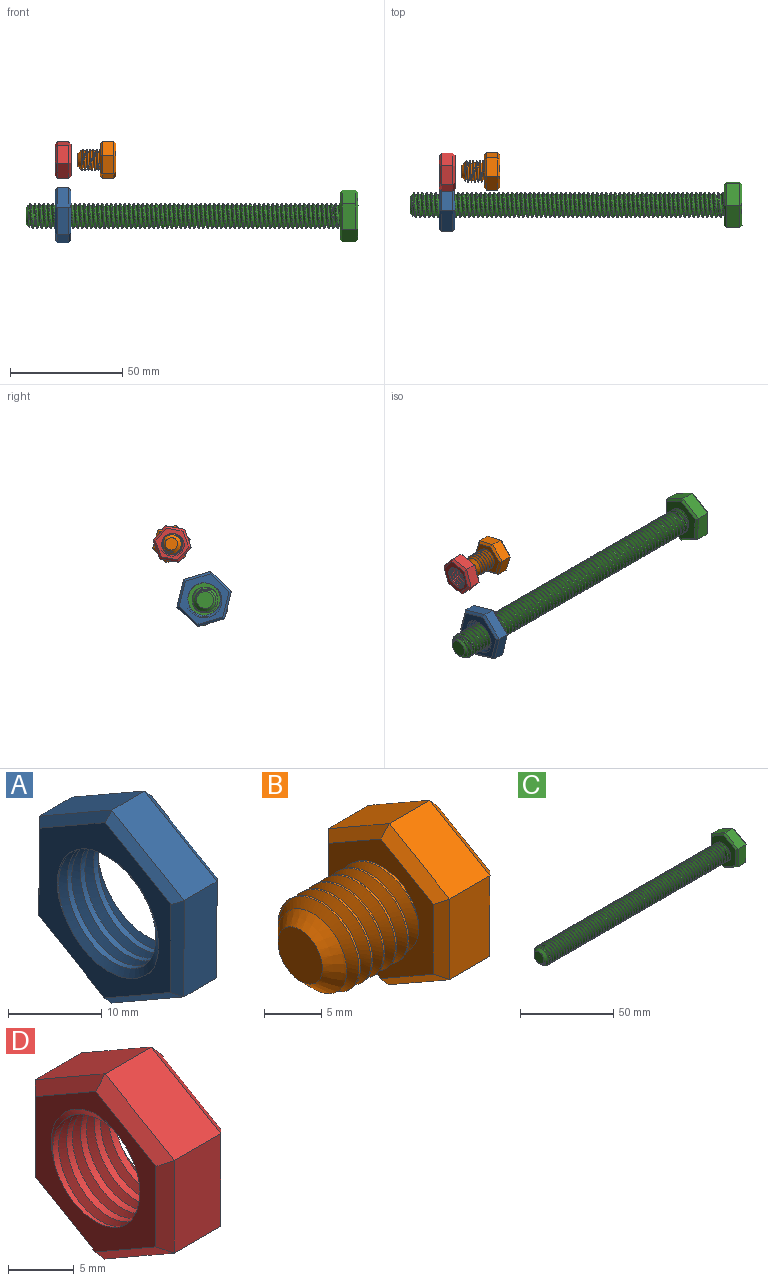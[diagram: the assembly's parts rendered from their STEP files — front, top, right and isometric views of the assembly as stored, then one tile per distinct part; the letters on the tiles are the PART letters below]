
ASSEMBLY  parts=4 mates=2
PART A: 23 faces, bbox 9.3x22.7x26 mm
  f0: cylinder r=7.24mm len=14.48mm, axis (1,0,0), area 111.6mm2, adj f7,f8,f21,f22
  f1: plane 10.98x6.38mm, normal (0,-0.5,0.86), area 63.5mm2, adj f2,f6,f14,f18
  f2: plane 12.7x5mm, normal (0,-1,0), area 63.5mm2, adj f1,f3,f12,f16
  f3: plane 11.02x6.32mm, normal (0,-0.5,-0.87), area 63.5mm2, adj f2,f4,f10,f15
  f4: plane 10.98x6.38mm, normal (0,0.5,-0.86), area 63.5mm2, adj f3,f5,f9,f17
  f5: plane 12.7x5mm, normal (0,1,0), area 63.5mm2, adj f4,f6,f11,f19
  f6: plane 11.02x6.32mm, normal (0,0.5,0.87), area 63.5mm2, adj f1,f5,f13,f20
  f7: plane 23.73x20.67mm, normal (-1,0,0), area 164.4mm2, adj f0,f9,f10,f11,f12,f13,f14,f21
  f8: plane 23.73x20.67mm, normal (1,0,0), area 164.4mm2, adj f0,f15,f16,f17,f18,f19,f20,f21
  f9: plane 10.99x6.96mm, normal (-0.71,0.36,-0.61), area 17.1mm2, adj f4,f7,f10,f11
  f10: plane 11.02x6.9mm, normal (-0.71,-0.35,-0.61), area 17.1mm2, adj f3,f7,f9,f12
  f11: plane 12.7x1.03mm, normal (-0.71,0.71,0), area 17.1mm2, adj f5,f7,f9,f13
  f12: plane 12.7x1.03mm, normal (-0.71,-0.71,0), area 17.1mm2, adj f2,f7,f10,f14
  f13: plane 11.02x6.9mm, normal (-0.71,0.35,0.61), area 17.1mm2, adj f6,f7,f11,f14
  f14: plane 10.99x6.96mm, normal (-0.71,-0.36,0.61), area 17.1mm2, adj f1,f7,f12,f13
  f15: plane 11.02x6.9mm, normal (0.71,-0.35,-0.61), area 17.1mm2, adj f3,f8,f16,f17
  f16: plane 12.7x1.03mm, normal (0.71,-0.71,0), area 17.1mm2, adj f2,f8,f15,f18
  f17: plane 10.99x6.96mm, normal (0.71,0.36,-0.61), area 17.1mm2, adj f4,f8,f15,f19
  f18: plane 10.99x6.96mm, normal (0.71,-0.36,0.61), area 17.1mm2, adj f1,f8,f16,f20
  f19: plane 12.7x1.03mm, normal (0.71,0.71,0), area 17.1mm2, adj f5,f8,f17,f20
  f20: plane 11.02x6.9mm, normal (0.71,0.35,0.61), area 17.1mm2, adj f6,f8,f18,f19
  f21: bspline ~19.31x16.73mm, area 223mm2, adj f0,f7,f8,f22
  f22: bspline ~19.31x16.73mm, area 223mm2, adj f0,f7,f8,f21
PART B: 25 faces, bbox 17.8x15.9x18.1 mm
  f0: cylinder r=4.75mm len=9.5mm, axis (1,0,0), area 28.1mm2, adj f1,f2,f4,f12
  f1: bspline ~10.97x9.91mm, area 196.7mm2, adj f0,f2,f4,f12
  f2: bspline ~10.97x10.66mm, area 196.6mm2, adj f0,f1,f4,f12
  f3: plane 5.5x5.5mm, normal (-1,0,0), area 23.8mm2, adj f4
  f4: cone r=4.75mm half-angle=45deg, axis (1,0,0), area 47.4mm2, adj f0,f1,f2,f3
  f5: plane 7.48x5mm, normal (0,-0.5,0.86), area 43.3mm2, adj f6,f10,f18,f22
  f6: plane 8.66x5mm, normal (0,-1,0), area 43.3mm2, adj f5,f7,f16,f20
  f7: plane 7.52x5mm, normal (0,-0.5,-0.87), area 43.3mm2, adj f6,f8,f14,f19
  f8: plane 7.48x5mm, normal (0,0.5,-0.86), area 43.3mm2, adj f7,f9,f13,f21
  f9: plane 8.66x5mm, normal (0,1,0), area 43.3mm2, adj f8,f10,f15,f23
  f10: plane 7.52x5mm, normal (0,0.5,0.87), area 43.3mm2, adj f5,f9,f17,f24
  f11: plane 15.01x13.03mm, normal (1,0,0), area 146.4mm2, adj f13,f14,f15,f16,f17,f18
  f12: plane 15.83x13.85mm, normal (-1,0,0), area 89.2mm2, adj f0,f1,f2,f19,f20,f21,f22,f23
  f13: plane 7.49x4.93mm, normal (0.71,0.36,-0.61), area 11.4mm2, adj f8,f11,f14,f15
  f14: plane 7.52x4.88mm, normal (0.71,-0.35,-0.61), area 11.4mm2, adj f7,f11,f13,f16
  f15: plane 8.66x1.03mm, normal (0.71,0.71,0), area 11.4mm2, adj f9,f11,f13,f17
  f16: plane 8.66x1.03mm, normal (0.71,-0.71,0), area 11.4mm2, adj f6,f11,f14,f18
  f17: plane 7.52x4.88mm, normal (0.71,0.35,0.61), area 11.4mm2, adj f10,f11,f15,f18
  f18: plane 7.49x4.93mm, normal (0.71,-0.36,0.61), area 11.4mm2, adj f5,f11,f16,f17
  f19: plane 7.52x4.88mm, normal (-0.71,-0.35,-0.61), area 11.4mm2, adj f7,f12,f20,f21
  f20: plane 8.66x1.03mm, normal (-0.71,-0.71,0), area 11.4mm2, adj f6,f12,f19,f22
  f21: plane 7.49x4.93mm, normal (-0.71,0.36,-0.61), area 11.4mm2, adj f8,f12,f19,f23
  f22: plane 7.49x4.93mm, normal (-0.71,-0.36,0.61), area 11.4mm2, adj f5,f12,f20,f24
  f23: plane 8.66x1.03mm, normal (-0.71,0.71,0), area 11.4mm2, adj f9,f12,f21,f24
  f24: plane 7.52x4.88mm, normal (-0.71,0.35,0.61), area 11.4mm2, adj f10,f12,f22,f23
PART C: 26 faces, bbox 149.6x21.1x24.2 mm
  f0: cylinder r=5.76mm len=138mm, axis (1,0,0), area -230.5mm2, adj f1,f2,f4,f5,f13
  f1: bspline ~140.88x13.3mm, area 3820.7mm2, adj f0,f2,f4,f5,f13
  f2: bspline ~141.54x13.3mm, area 3821.3mm2, adj f0,f1,f4,f13
  f3: plane 7.52x7.52mm, normal (-1,0,0), area 44.4mm2, adj f4
  f4: cone r=5.76mm half-angle=45deg, axis (1,0,0), area 53.1mm2, adj f0,f1,f2,f3,f5
  f5: cone r=5.76mm half-angle=45deg, axis (1,0,0), area 0.5mm2, adj f0,f1,f4
  f6: plane 9.98x6mm, normal (0,-0.5,0.86), area 69.3mm2, adj f7,f11,f19,f23
  f7: plane 11.55x6mm, normal (0,-1,0), area 69.3mm2, adj f6,f8,f17,f21
  f8: plane 10.02x6mm, normal (0,-0.5,-0.87), area 69.3mm2, adj f7,f9,f15,f20
  f9: plane 9.98x6mm, normal (0,0.5,-0.86), area 69.3mm2, adj f8,f10,f14,f22
  f10: plane 11.55x6mm, normal (0,1,0), area 69.3mm2, adj f9,f11,f16,f24
  f11: plane 10.02x6mm, normal (0,0.5,0.87), area 69.3mm2, adj f6,f10,f18,f25
  f12: plane 20.78x18.04mm, normal (1,0,0), area 280.6mm2, adj f14,f15,f16,f17,f18,f19
  f13: plane 21.88x19.13mm, normal (-1,0,0), area 198.3mm2, adj f0,f1,f2,f20,f21,f22,f23,f24
  f14: plane 9.98x6.38mm, normal (0.71,0.36,-0.61), area 15.5mm2, adj f9,f12,f15,f16
  f15: plane 10.02x6.32mm, normal (0.71,-0.35,-0.61), area 15.5mm2, adj f8,f12,f14,f17
  f16: plane 11.55x1.04mm, normal (0.71,0.71,0), area 15.5mm2, adj f10,f12,f14,f18
  f17: plane 11.55x1.04mm, normal (0.71,-0.71,0), area 15.5mm2, adj f7,f12,f15,f19
  f18: plane 10.02x6.32mm, normal (0.71,0.35,0.61), area 15.5mm2, adj f11,f12,f16,f19
  f19: plane 9.98x6.38mm, normal (0.71,-0.36,0.61), area 15.5mm2, adj f6,f12,f17,f18
  f20: plane 10.02x6.32mm, normal (-0.71,-0.35,-0.61), area 15.5mm2, adj f8,f13,f21,f22
  f21: plane 11.55x1.04mm, normal (-0.71,-0.71,0), area 15.5mm2, adj f7,f13,f20,f23
  f22: plane 9.98x6.38mm, normal (-0.71,0.36,-0.61), area 15.5mm2, adj f9,f13,f20,f24
  f23: plane 9.98x6.38mm, normal (-0.71,-0.36,0.61), area 15.5mm2, adj f6,f13,f21,f25
  f24: plane 11.55x1.04mm, normal (-0.71,0.71,0), area 15.5mm2, adj f10,f13,f22,f25
  f25: plane 10.02x6.32mm, normal (-0.71,0.35,0.61), area 15.5mm2, adj f11,f13,f23,f24
PART D: 23 faces, bbox 9.1x15.4x17.7 mm
  f0: plane 7.49x5mm, normal (0,-0.5,0.86), area 43.3mm2, adj f1,f5,f13,f17
  f1: plane 8.66x5mm, normal (0,-1,0), area 43.3mm2, adj f0,f2,f11,f15
  f2: plane 7.51x5mm, normal (0,-0.5,-0.87), area 43.3mm2, adj f1,f3,f9,f14
  f3: plane 7.49x5mm, normal (0,0.5,-0.86), area 43.3mm2, adj f2,f4,f8,f16
  f4: plane 8.66x5mm, normal (0,1,0), area 43.3mm2, adj f3,f5,f10,f18
  f5: plane 7.51x5mm, normal (0,0.5,0.87), area 43.3mm2, adj f0,f4,f12,f19
  f6: plane 15.37x13.38mm, normal (-1,0,0), area 71.4mm2, adj f8,f9,f10,f11,f12,f13,f20,f21
  f7: plane 15.37x13.38mm, normal (1,0,0), area 71.4mm2, adj f14,f15,f16,f17,f18,f19,f20,f21
  f8: plane 7.49x4.93mm, normal (-0.71,0.36,-0.61), area 11.4mm2, adj f3,f6,f9,f10
  f9: plane 7.51x4.89mm, normal (-0.71,-0.35,-0.61), area 11.4mm2, adj f2,f6,f8,f11
  f10: plane 8.66x1.02mm, normal (-0.71,0.71,0), area 11.4mm2, adj f4,f6,f8,f12
  f11: plane 8.66x1.02mm, normal (-0.71,-0.71,0), area 11.4mm2, adj f1,f6,f9,f13
  f12: plane 7.51x4.89mm, normal (-0.71,0.35,0.61), area 11.4mm2, adj f5,f6,f10,f13
  f13: plane 7.49x4.93mm, normal (-0.71,-0.36,0.61), area 11.4mm2, adj f0,f6,f11,f12
  f14: plane 7.51x4.89mm, normal (0.71,-0.35,-0.61), area 11.4mm2, adj f2,f7,f15,f16
  f15: plane 8.66x1.02mm, normal (0.71,-0.71,0), area 11.4mm2, adj f1,f7,f14,f17
  f16: plane 7.49x4.93mm, normal (0.71,0.36,-0.61), area 11.4mm2, adj f3,f7,f14,f18
  f17: plane 7.49x4.93mm, normal (0.71,-0.36,0.61), area 11.4mm2, adj f0,f7,f15,f19
  f18: plane 8.66x1.02mm, normal (0.71,0.71,0), area 11.4mm2, adj f4,f7,f16,f19
  f19: plane 7.51x4.89mm, normal (0.71,0.35,0.61), area 11.4mm2, adj f5,f7,f17,f18
  f20: cylinder r=4.66mm len=9.32mm, axis (1,0,0), area 85.4mm2, adj f6,f7,f21,f22
  f21: bspline ~12.5x10.82mm, area 128.4mm2, adj f6,f7,f20,f22
  f22: bspline ~12.5x10.82mm, area 128.5mm2, adj f6,f7,f20,f21
PLACE A rot(axis=(0,0.6,-0.8),180deg) t=(-55.27,-6.86,23.48)mm fixed
PLACE B rot(axis=(-1,0,0),43.8deg) t=(-31.66,7.73,48.08)mm
PLACE C rot(axis=(-1,0,0),178.1deg) t=(75.73,-7.25,23.06)mm
PLACE D rot(axis=(1,0,0),100.2deg) t=(-48.16,7.38,48.02)mm fixed
MATE cylindrical C.f0 <-> A.f7  axis (-1,0,0) through (-68.27,-7.25,23.06)mm
MATE cylindrical B.f0 <-> D.f6  axis (-1,0,0) through (-45.16,7.73,48.08)mm
